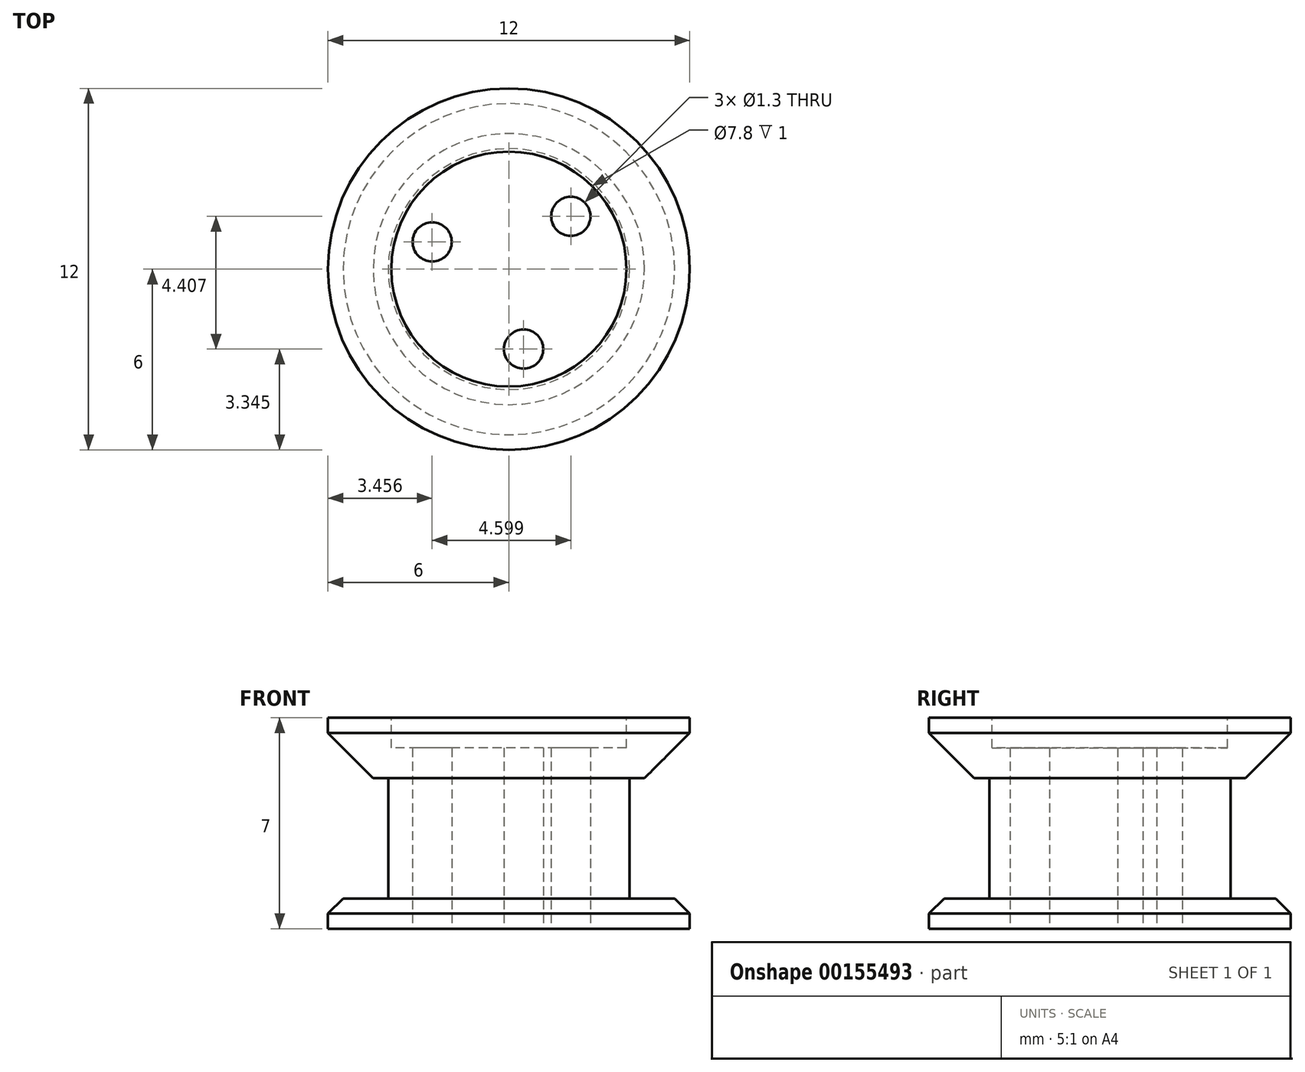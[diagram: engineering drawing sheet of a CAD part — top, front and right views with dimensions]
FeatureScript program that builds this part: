
annotation { "Feature Type Name" : "Feature", "Feature Type Description" : "" }
export const myFeature = defineFeature(function(context is Context, id is Id, definition is map)
    precondition{}
    {
        {
            var Q0;
            Q0=qCreatedBy(makeId("Top.planeOp"),FACE);
            var sketch = newSketch(context, id + "F0", { "sketchPlane" : qUnion([Q0])});
            skCircle(sketch, "E0", {"center": v(0, 0) * mm, "radius": 6 * mm});
            skCircle(sketch, "E1", {"center": v(0, 0) * mm, "radius": 4 * mm});
            skCircle(sketch, "E2.cCircle", {"center": v(0, 0) * mm, "radius": 2.7 * mm, "construction": true});
            skLineSegment(sketch, "E2.0", {"start": v(0.49, -2.66) * mm, "end": v(-2.54, 0.9) * mm});
            skLineSegment(sketch, "E2.1", {"start": v(-2.54, 0.9) * mm, "end": v(2.05, 1.75) * mm});
            skLineSegment(sketch, "E2.2", {"start": v(2.05, 1.75) * mm, "end": v(0.49, -2.66) * mm});
            skCircle(sketch, "E3", {"center": v(0.49, -2.66) * mm, "radius": 0.65 * mm});
            skCircle(sketch, "E4", {"center": v(2.05, 1.75) * mm, "radius": 0.65 * mm});
            skCircle(sketch, "E5", {"center": v(-2.54, 0.9) * mm, "radius": 0.65 * mm});
            skSolve(sketch);
        }
        {
            var Q0;
            Q0=makeQuery(id+"F0.imprint","IMPRINT",FACE,{"disambiguationData":[TD([[makeQuery(id+"F0.imprint","IMPRINT",EDGE,{"derivedFrom":sQuery(id+"F0.wireOp",EDGE,"E0")}),1.0]])]});
            extrude(context, id + "F1", {"entities" : qUnion([Q0]), "depth" : 1 * mm});
        }
        {
            var Q0;
            Q0=makeQuery(id+"F0.imprint","IMPRINT",FACE,{"disambiguationData":[TD([[makeQuery(id+"F0.imprint","IMPRINT",EDGE,{"derivedFrom":sQuery(id+"F0.wireOp",EDGE,"E1")}),1.0]])]});
            var Q1;
            {var subQ0=sQuery(id+"F0.wireOp",EDGE,"E3");var subQ1=sQuery(id+"F0.wireOp",EDGE,"E2.0");var subQ2=makeQuery(id+"F0.imprint","INTERSECT",VERTEX,{"derivedFrom":[subQ1,subQ0]});Q1=makeQuery(id+"F0.imprint","IMPRINT",FACE,{"disambiguationData":[TD([[makeQuery(id+"F0.imprint","IMPRINT",EDGE,{"disambiguationData":[TD([[subQ2,-1.0]])],"derivedFrom":subQ1}),-1.0]])]});}
            extrude(context, id + "F2", {"entities" : qUnion([Q0, Q1]), "operationType" : NewBodyOperationType.ADD, "depth" : 7 * mm});
        }
        {
            var Q0;
            Q0=makeQuery(id+"F2.opExtrude","CAP_FACE",FACE,{"disambiguationData":[OSD([sQuery(id+"F0.wireOp",EDGE,"E1"),sQuery(id+"F0.wireOp",EDGE,"E3"),sQuery(id+"F0.wireOp",EDGE,"E4"),sQuery(id+"F0.wireOp",EDGE,"E5")])],"isStart":false});
            var sketch = newSketch(context, id + "F3", { "sketchPlane" : qUnion([Q0])});
            skCircle(sketch, "E6", {"center": v(0, 0) * mm, "radius": 6 * mm});
            skCircle(sketch, "E7", {"center": v(0, 0) * mm, "radius": 3.9 * mm});
            skSolve(sketch);
        }
        {
            var Q0;
            Q0=makeQuery(id+"F3.imprint","IMPRINT",FACE,{"disambiguationData":[TD([[makeQuery(id+"F3.imprint","IMPRINT",EDGE,{"derivedFrom":sQuery(id+"F3.wireOp",EDGE,"E6")}),1.0]])]});
            extrude(context, id + "F4", {"entities" : qUnion([Q0]), "operationType" : NewBodyOperationType.ADD, "oppositeDirection" : true, "depth" : 2 * mm});
        }
        {
            var Q0;
            Q0=makeQuery(id+"F3.imprint","IMPRINT",FACE,{"disambiguationData":[TD([[makeQuery(id+"F3.imprint","IMPRINT",EDGE,{"derivedFrom":sQuery(id+"F3.wireOp",EDGE,"E7")}),1.0]])]});
            extrude(context, id + "F5", {"entities" : qUnion([Q0]), "operationType" : NewBodyOperationType.REMOVE, "oppositeDirection" : true, "depth" : 1 * mm});
        }
        {
            var Q0;
            Q0=makeQuery(id+"F4.opExtrude","CAP_EDGE",EDGE,{"disambiguationData":[OSD([sQuery(id+"F3.wireOp",EDGE,"E6")])],"isStart":false});
            chamfer(context, id + "F6", {"entities" : qUnion([Q0]), "width" : 1.5 * mm, "tangentPropagation" : true});
        }
        {
            var Q0;
            Q0=makeQuery(id+"F1.opExtrude","CAP_EDGE",EDGE,{"disambiguationData":[OSD([sQuery(id+"F0.wireOp",EDGE,"E0")])],"isStart":false});
            chamfer(context, id + "F7", {"entities" : qUnion([Q0]), "width" : 0.5 * mm, "tangentPropagation" : true});
        }
    });
